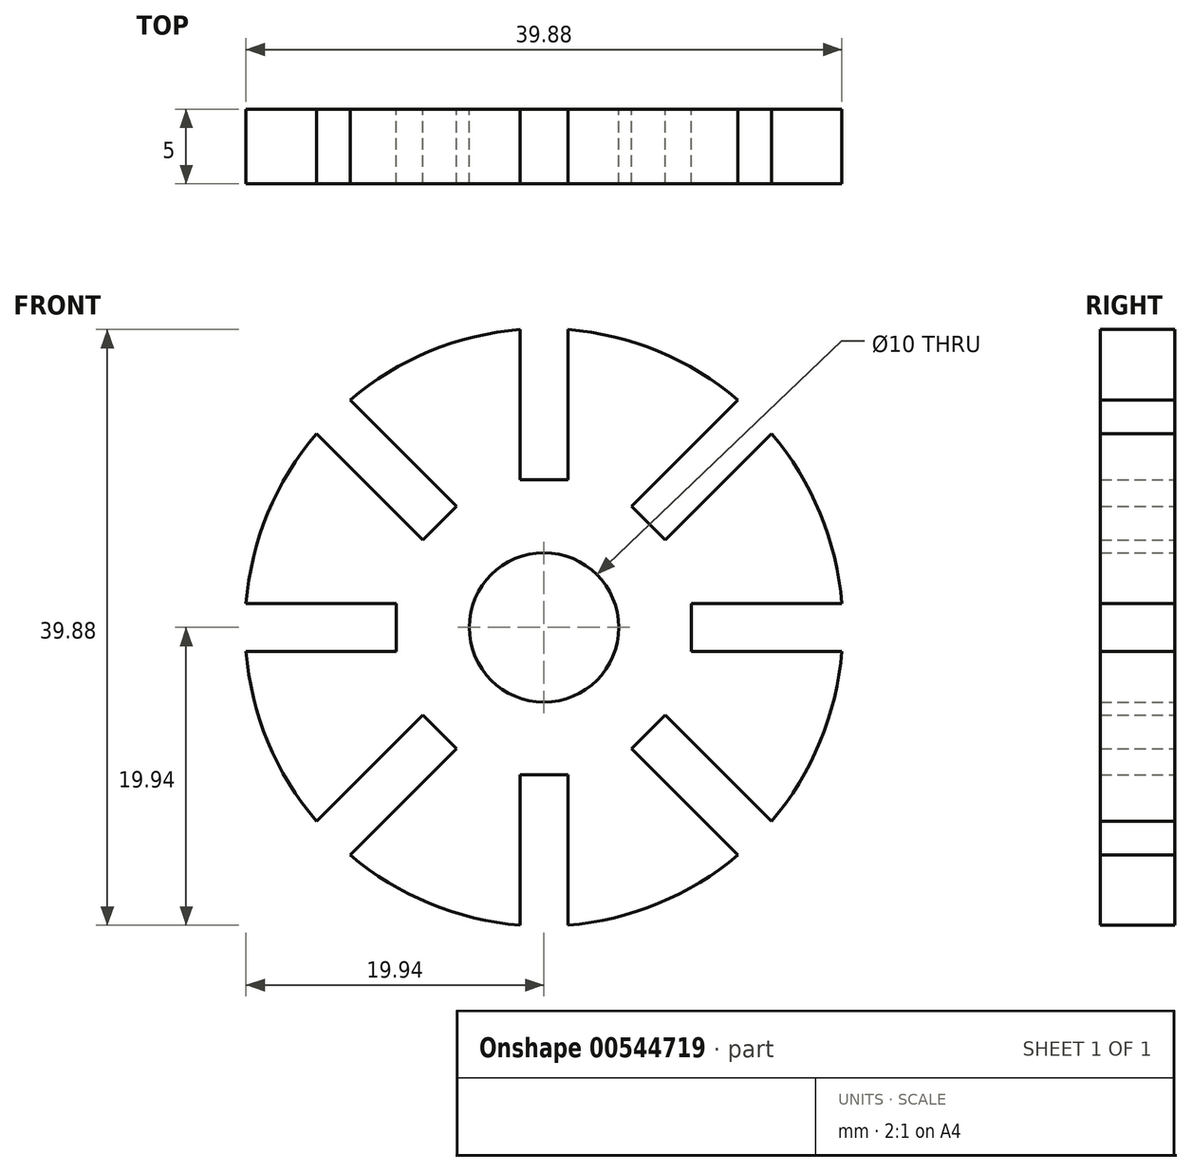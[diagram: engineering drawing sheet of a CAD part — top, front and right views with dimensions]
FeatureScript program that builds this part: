
annotation { "Feature Type Name" : "Feature", "Feature Type Description" : "" }
export const myFeature = defineFeature(function(context is Context, id is Id, definition is map)
    precondition{}
    {
        {
            var Q0;
            Q0=qCreatedBy(makeId("Front.planeOp"),FACE);
            var sketch = newSketch(context, id + "F0", { "sketchPlane" : qUnion([Q0])});
            skArc(sketch, "E0", {"start": v(53.84, 19.94) * mm, "mid": v(47.79, 18.48) * mm, "end": v(42.47, 15.23) * mm});
            skCircle(sketch, "E1", {"center": v(55.44, 0) * mm, "radius": 5 * mm});
            skLineSegment(sketch, "E2", {"start": v(55.44, 0) * mm, "end": v(55.44, 26.46) * mm, "construction": true});
            skLineSegment(sketch, "E3.bottom", {"start": v(57.04, 9.87) * mm, "end": v(53.84, 9.87) * mm});
            skLineSegment(sketch, "E3.left", {"start": v(57.04, 9.87) * mm, "end": v(57.04, 19.94) * mm});
            skLineSegment(sketch, "E3.right", {"start": v(53.84, 9.87) * mm, "end": v(53.84, 19.94) * mm});
            skPoint(sketch, "E3.middle", {"position": v(55.44, 20) * mm});
            skPoint(sketch, "E3.top.end.orphan", {"position": v(53.84, 30.13) * mm});
            skPoint(sketch, "E3.top.start.orphan", {"position": v(57.04, 30.13) * mm});
            skLineSegment(sketch, "E4.1.0", {"start": v(47.33, 5.85) * mm, "end": v(40.21, 12.97) * mm});
            skLineSegment(sketch, "E4.1.1", {"start": v(49.6, 8.11) * mm, "end": v(42.47, 15.23) * mm});
            skLineSegment(sketch, "E4.1.2", {"start": v(49.6, 8.11) * mm, "end": v(47.33, 5.85) * mm});
            skLineSegment(sketch, "E4.2.0", {"start": v(45.57, -1.6) * mm, "end": v(35.5, -1.6) * mm});
            skLineSegment(sketch, "E4.2.1", {"start": v(45.57, 1.6) * mm, "end": v(35.5, 1.6) * mm});
            skLineSegment(sketch, "E4.2.2", {"start": v(45.57, 1.6) * mm, "end": v(45.57, -1.6) * mm});
            skLineSegment(sketch, "E4.3.0", {"start": v(49.6, -8.11) * mm, "end": v(42.47, -15.23) * mm});
            skLineSegment(sketch, "E4.3.1", {"start": v(47.33, -5.85) * mm, "end": v(40.21, -12.97) * mm});
            skLineSegment(sketch, "E4.3.2", {"start": v(47.33, -5.85) * mm, "end": v(49.6, -8.11) * mm});
            skLineSegment(sketch, "E4.4.0", {"start": v(57.04, -9.87) * mm, "end": v(57.04, -19.94) * mm});
            skLineSegment(sketch, "E4.4.1", {"start": v(53.84, -9.87) * mm, "end": v(53.84, -19.94) * mm});
            skLineSegment(sketch, "E4.4.2", {"start": v(53.84, -9.87) * mm, "end": v(57.04, -9.87) * mm});
            skLineSegment(sketch, "E4.5.0", {"start": v(63.55, -5.85) * mm, "end": v(70.67, -12.97) * mm});
            skLineSegment(sketch, "E4.5.1", {"start": v(61.29, -8.11) * mm, "end": v(68.4, -15.23) * mm});
            skLineSegment(sketch, "E4.5.2", {"start": v(61.29, -8.11) * mm, "end": v(63.55, -5.85) * mm});
            skLineSegment(sketch, "E4.6.0", {"start": v(65.31, 1.6) * mm, "end": v(75.38, 1.6) * mm});
            skLineSegment(sketch, "E4.6.1", {"start": v(65.31, -1.6) * mm, "end": v(75.38, -1.6) * mm});
            skLineSegment(sketch, "E4.6.2", {"start": v(65.31, -1.6) * mm, "end": v(65.31, 1.6) * mm});
            skLineSegment(sketch, "E4.7.0", {"start": v(61.29, 8.11) * mm, "end": v(68.4, 15.23) * mm});
            skLineSegment(sketch, "E4.7.1", {"start": v(63.55, 5.85) * mm, "end": v(70.67, 12.97) * mm});
            skLineSegment(sketch, "E4.7.2", {"start": v(63.55, 5.85) * mm, "end": v(61.29, 8.11) * mm});
            skArc(sketch, "E5.trimOffspring", {"start": v(40.21, 12.97) * mm, "mid": v(36.96, 7.65) * mm, "end": v(35.5, 1.6) * mm});
            skArc(sketch, "E6.trimOffspring", {"start": v(35.5, -1.6) * mm, "mid": v(36.96, -7.65) * mm, "end": v(40.21, -12.97) * mm});
            skArc(sketch, "E7.trimOffspring", {"start": v(42.47, -15.23) * mm, "mid": v(47.79, -18.48) * mm, "end": v(53.84, -19.94) * mm});
            skArc(sketch, "E8.trimOffspring", {"start": v(57.04, -19.94) * mm, "mid": v(63.1, -18.48) * mm, "end": v(68.4, -15.23) * mm});
            skArc(sketch, "E9.trimOffspring", {"start": v(70.67, -12.97) * mm, "mid": v(73.92, -7.65) * mm, "end": v(75.38, -1.6) * mm});
            skArc(sketch, "E10.trimOffspring", {"start": v(75.38, 1.6) * mm, "mid": v(73.92, 7.65) * mm, "end": v(70.67, 12.97) * mm});
            skArc(sketch, "E11.trimOffspring", {"start": v(68.4, 15.23) * mm, "mid": v(63.1, 18.48) * mm, "end": v(57.04, 19.94) * mm});
            skSolve(sketch);
        }
        {
            var Q0;
            Q0=qSketchRegion(id+"F0",true);
            extrude(context, id + "F1", {"entities" : qUnion([Q0]), "depth" : 5 * mm, "offsetDistance" : 25 * mm});
        }
        {
            var Q0;
            Q0=qSketchRegion(id+"F0",true);
            extrude(context, id + "F2", {"entities" : qUnion([Q0]), "operationType" : NewBodyOperationType.ADD, "depth" : 5 * mm, "offsetDistance" : 25 * mm});
        }
    });
